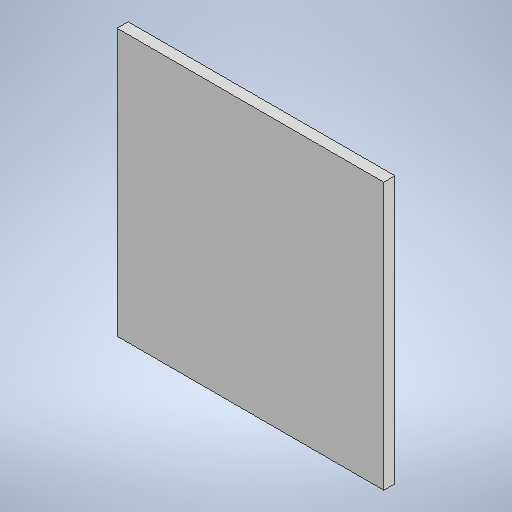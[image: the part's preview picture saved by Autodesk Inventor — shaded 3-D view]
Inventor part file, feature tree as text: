
AUTODESK INVENTOR PART (.ipt)
format: ipt  version: 2025.1 (Build 291241020, 241B)  size: 201,216 bytes
history: native  units: in
note: dims shown in document units (in); Inventor stores cm internally (conversion verified against a paired STEP export)
features: extrude x1, sketch x1
ambient origin geometry x8: Origin, YZ Plane, XZ Plane, XY Plane, X Axis, Y Axis, Z Axis, Center Point
bodies: Solid1 (feature_tree)
feature tree (2):
  extrude  "Extrusion1"  Depth=6.0in
  sketch  "Sketch1"  dims[d0=6.0in d1=6.0in d2=0.25in d3=0.0in]
